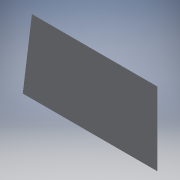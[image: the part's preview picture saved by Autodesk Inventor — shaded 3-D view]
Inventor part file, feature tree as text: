
AUTODESK INVENTOR PART (.ipt)
format: ipt  version: 2017 (Build 210142000, 142)  size: 92,160 bytes
history: native  units: mm
features: extrude x1, sketch x1
ambient origin geometry x8: Origin, YZ Plane, XZ Plane, XY Plane, X Axis, Y Axis, Z Axis, Center Point
bodies: Volumenkörper1 (feature_tree)
feature tree (2):
  extrude  "Extrusion1"  Depth=44000.0mm
  sketch  "Skizze1"  dims[d0=1.0mm d1=0.0mm d2=44000.0mm d3=24000.0mm d4=41000.0mm]
